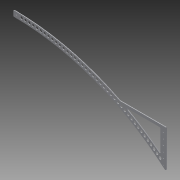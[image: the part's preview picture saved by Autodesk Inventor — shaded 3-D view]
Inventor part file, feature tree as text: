
AUTODESK INVENTOR PART (.ipt)
format: ipt  version: 2014 (Build 180170000, 170)  size: 238,080 bytes
history: native  units: in
note: dims shown in document units (in); Inventor stores cm internally (conversion verified against a paired STEP export)
features: extrude x5, sketch x5, fillet x1
ambient origin geometry x8: Origin, YZ Plane, XZ Plane, XY Plane, X Axis, Y Axis, Z Axis, Center Point
bodies: Solid1 (feature_tree)
feature tree (11):
  extrude  "Extrusion1"  Depth=4.0in
  extrude  "Extrusion2"  Depth=5.0in
  extrude  "Extrusion3"  Depth=0.125in
  extrude  "Extrusion4"  Depth=0.125in
  extrude  "Extrusion5"  Depth=0.125in
  fillet  "Fillet1"  Radius=0.163in
  sketch  "Sketch1"  dims[d2=13.5in d3=4.0in]
  sketch  "Sketch2"  dims[d4=1.75in d6=5.0in]
  sketch  "Sketch3"  dims[d7=1.0in d9=0.125in]
  sketch  "Sketch4"  dims[d10=0.125in d11=0.0in d12=0.163in]
  sketch  "Sketch5"  dims[d13=0.5in d14=3.5in d15=0.163in d17=6.5in d18=1.0in d19=0.0in d20=27.0in d21=25.875in d22=0.125in d23=26.5in d24=0.5in d25=41.26in d26=0.0137in d27=0.2762in d28=15.748in d30=0.2542in d32=1.0in d33=0.0in d34=0.163in d35=0.5in d36=5.0in d38=6.0in d39=1.0in d40=0.5in d41=0.125in d42=0.0in d43=1.9685in d45=1.0in d46=0.3937in d48=1.0in d50=0.125in d51=0.0in d52=0.125in]
